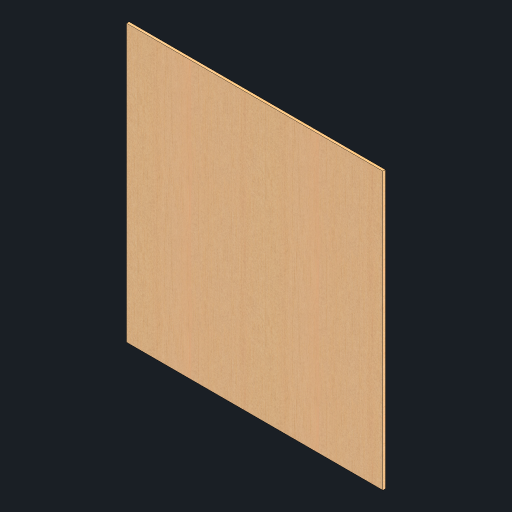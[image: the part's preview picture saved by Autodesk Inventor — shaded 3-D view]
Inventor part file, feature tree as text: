
AUTODESK INVENTOR PART (.ipt)
format: ipt  version: 2024.1 (Build 281209000, 209)  size: 311,808 bytes
history: native  units: mm
features: other x2, extrude x1, sketch x1
ambient origin geometry x8: Origin, YZ Plane, XZ Plane, XY Plane, X Axis, Y Axis, Z Axis, Center Point
bodies: Body1 (feature_tree)
feature tree (4):
  other  "솔리드1"
  extrude  "돌출1"  Depth=510.0mm
  sketch  "스케치1"
  other  "Finish1"
